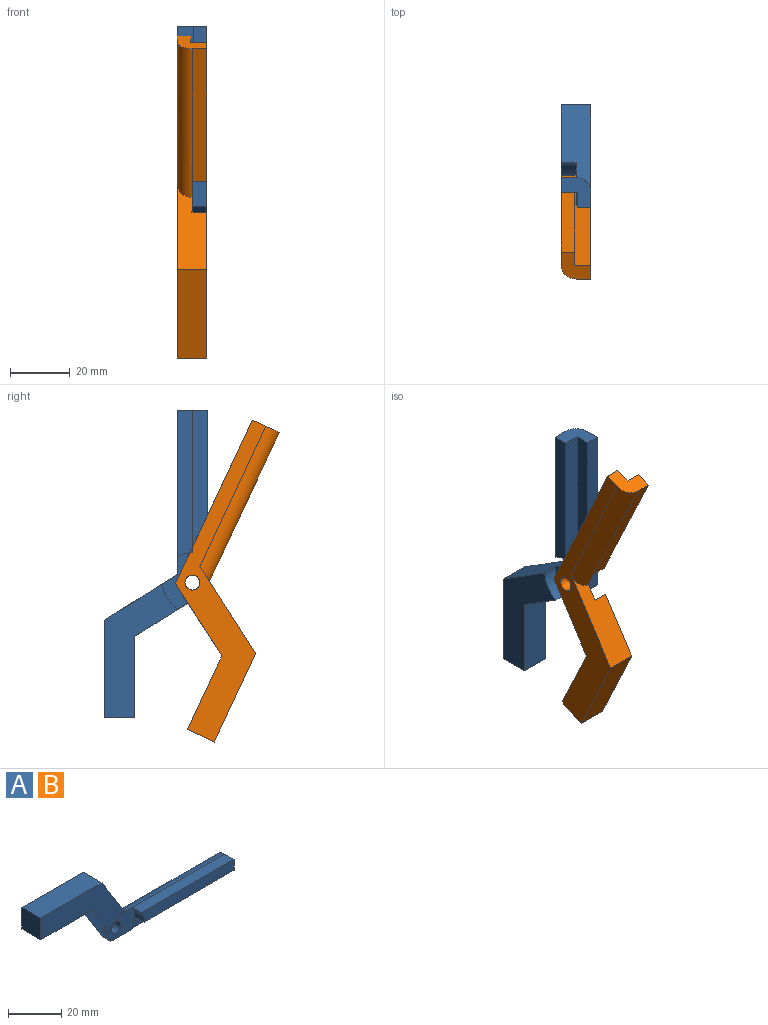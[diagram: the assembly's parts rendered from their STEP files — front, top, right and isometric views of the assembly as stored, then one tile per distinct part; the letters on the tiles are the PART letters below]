
ASSEMBLY  parts=2 mates=1
PART A: 19 faces, bbox 103.1x10x34.4 mm
  f0: plane 10x10mm, normal (1,0,0), area 67.7mm2, adj f1,f2,f7,f10,f15,f17,f18
  f1: plane 60.6x5mm, normal (0,0,-1), area 284.2mm2, adj f0,f3,f7,f14,f16,f17
  f2: plane 49.18x5mm, normal (0,-1,0), area 241.3mm2, adj f0,f10,f12,f15
  f3: plane 24.36x15.31mm, normal (-0.85,0,-0.53), area 230.6mm2, adj f1,f7,f8,f9,f13,f14
  f4: plane 29.36x18.46mm, normal (0.85,0,0.53), area 264.6mm2, adj f7,f8,f11,f13,f14,f18
  f5: cylinder r=2.5mm len=5mm, axis (0,-1,0), area 78.5mm2, adj f7,f14
  f6: plane 10x10mm, normal (-1,0,0), area 100mm2, adj f7,f8,f9,f11
  f7: plane 103.06x34.36mm, normal (0,1,0), area 878.1mm2, adj f0,f1,f3,f4,f5,f6,f9,f11
  f8: plane 44.85x24.69mm, normal (0,-1,0), area 491.2mm2, adj f3,f4,f6,f9,f11,f13
  f9: plane 27.15x10mm, normal (0,0,-1), area 271.5mm2, adj f3,f6,f7,f8
  f10: plane 49.18x5mm, normal (0,0,1), area 245.9mm2, adj f0,f2,f12,f18
  f11: plane 32.67x10mm, normal (0,0,1), area 326.7mm2, adj f4,f6,f7,f8
  f12: cylinder r=10mm len=5mm, axis (0,-1,0), area 26.2mm2, adj f2,f10,f14,f15
  f13: cylinder r=10mm len=8.47mm, axis (0,-1,0), area 52.4mm2, adj f3,f4,f8,f14
  f14: plane 18.84x14.99mm, normal (0,-1,0), area 171.7mm2, adj f1,f3,f4,f5,f12,f13,f16,f18
  f15: plane 47.84x5.38mm, normal (0,0,-1), area 257.4mm2, adj f0,f2,f12,f16,f17
  f16: cylinder r=10mm len=5mm, axis (0,-1,0), area 2mm2, adj f1,f14,f15,f17
  f17: plane 49.18x5mm, normal (0,-1,0), area 241.3mm2, adj f0,f1,f15,f16
  f18: cylinder r=5mm len=55.07mm, axis (-1,0,0), area 423.6mm2, adj f0,f4,f7,f10,f14
PART B: same geometry as A
PLACE A rot(axis=(-0.58,-0.58,-0.58),120deg) t=(15.08,2.46,-1.16)mm
PLACE B rot(axis=(0.65,-0.65,0.41),135.4deg) t=(15.08,2.46,-1.16)mm
MATE revolute A.f5 <-> B.f5  axis (1,0,0) through (20.08,2.46,-1.16)mm
